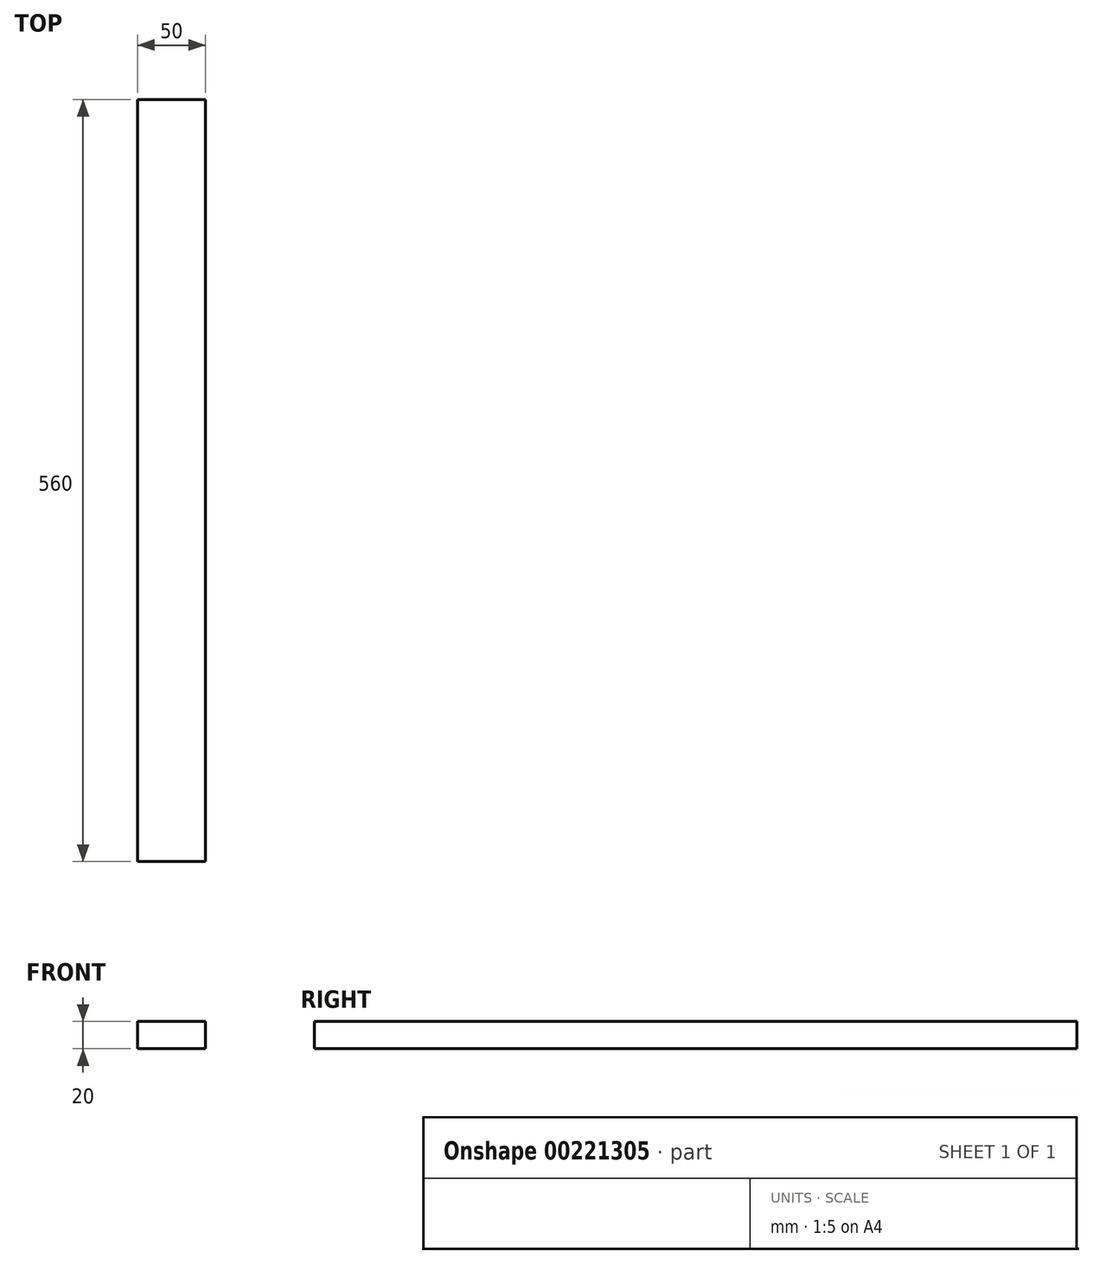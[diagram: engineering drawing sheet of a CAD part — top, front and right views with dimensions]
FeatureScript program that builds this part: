
annotation { "Feature Type Name" : "Feature", "Feature Type Description" : "" }
export const myFeature = defineFeature(function(context is Context, id is Id, definition is map)
    precondition{}
    {
        {
            var Q0;
            Q0=qCreatedBy(makeId("Front.planeOp"),FACE);
            var sketch = newSketch(context, id + "F0", { "sketchPlane" : qUnion([Q0])});
            skLineSegment(sketch, "E0.bottom", {"start": v(-21.52, 12.77) * mm, "end": v(28.48, 12.77) * mm});
            skLineSegment(sketch, "E0.top", {"start": v(-21.52, -7.23) * mm, "end": v(28.48, -7.23) * mm});
            skLineSegment(sketch, "E0.left", {"start": v(-21.52, 12.77) * mm, "end": v(-21.52, -7.23) * mm});
            skLineSegment(sketch, "E0.right", {"start": v(28.48, 12.77) * mm, "end": v(28.48, -7.23) * mm});
            skSolve(sketch);
        }
        {
            var Q0;
            Q0=makeQuery(id+"F0.imprint","IMPRINT",FACE,{"disambiguationData":[TD([[makeQuery(id+"F0.imprint","IMPRINT",EDGE,{"derivedFrom":sQuery(id+"F0.wireOp",EDGE,"E0.bottom")}),-1.0]])]});
            extrude(context, id + "F1", {"entities" : qUnion([Q0]), "oppositeDirection" : true, "depth" : 560 * mm});
        }
    });
